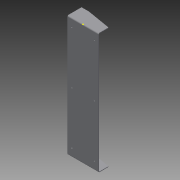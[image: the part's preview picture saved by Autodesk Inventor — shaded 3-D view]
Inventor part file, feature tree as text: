
AUTODESK INVENTOR PART (.ipt)
format: ipt  version: 2015 (Build 190159000, 159)  size: 184,832 bytes
history: native  units: mm
features: other x6, hole x6, sheet_metal_op x4, chamfer x4, sketch x4, mirror x1
ambient origin geometry x8: Origin, YZ Plane, XZ Plane, XY Plane, X Axis, Y Axis, Z Axis, Center Point
bodies: Solid1 (feature_tree)
feature tree (25):
  sheet_metal_op  "Face1"
  sheet_metal_op  "Flange1"
  other  "A-Side Definition"
  other  "Corner Chamfer1"
  chamfer  "Corner Round1"
  chamfer  "Corner Round2"
  mirror  "Mirror1"
  other  "Corner Chamfer2"
  chamfer  "Corner Round3"
  chamfer  "Corner Round5"
  hole  "Hole1"  [1 undecoded]
  hole  "Hole2"  [1 undecoded]
  hole  "Hole3"  [1 undecoded]
  hole  "Hole4"  [1 undecoded]
  hole  "Hole5"  [1 undecoded]
  hole  "Hole6"  [1 undecoded]
  sketch  "Sketch3"  dims[d4=0.75mm d5=3.0mm]
  sketch  "Sketch4"  dims[d6=1.5mm d7=35.0mm d8=90.0deg d9=1.5mm d10=6.0mm d11=1.5mm d12=1.5mm d13=10.0mm d14=58.5mm d15=45.0deg d16=0.25mm d17=0.25mm d18=58.5mm d19=10.0mm d20=45.0deg d21=0.25mm d23=0.25mm d24=17.0mm d25=10.5mm d26=3.2mm d27=6.0mm d28=4.0mm d29=2.0mm d30=90.0deg d31=1.5mm d32=20.594885mm d33=10.5mm d34=17.0mm d35=3.2mm d36=6.0mm d37=4.0mm d38=2.0mm d39=90.0deg d40=1.5mm d41=20.594885mm d42=17.0mm d43=10.5mm d44=3.2mm d45=6.0mm d46=4.0mm d47=2.0mm d48=90.0deg d49=1.5mm d50=20.594885mm d51=17.0mm d52=10.5mm d53=3.2mm d54=6.0mm d55=4.0mm d56=2.0mm d57=90.0deg d58=1.5mm d59=20.594885mm d60=10.5mm d61=147.0mm d62=3.2mm d63=6.0mm d64=4.0mm d65=2.0mm d66=90.0deg d67=1.5mm d68=20.594885mm d69=10.5mm d70=147.0mm d71=3.2mm d72=6.0mm d73=4.0mm d74=2.0mm d75=90.0deg d76=1.5mm d77=20.594885mm]
  sketch  "Sketch1"  dims[d0=77.0mm d1=147.0mm]
  other  "Plate1"
  sketch  "Sketch2"  dims[d2=1.5mm d3=1.5mm]
  other  "Plate2"
  sheet_metal_op  "Bend1"
  sheet_metal_op  "Corner1"
  other  "Definition1"
note: 6 required parameter values undecoded (feature->parameter linkage not recoverable at this tier; creation-order binding heuristic only, values carry confidence <= 0.55)
